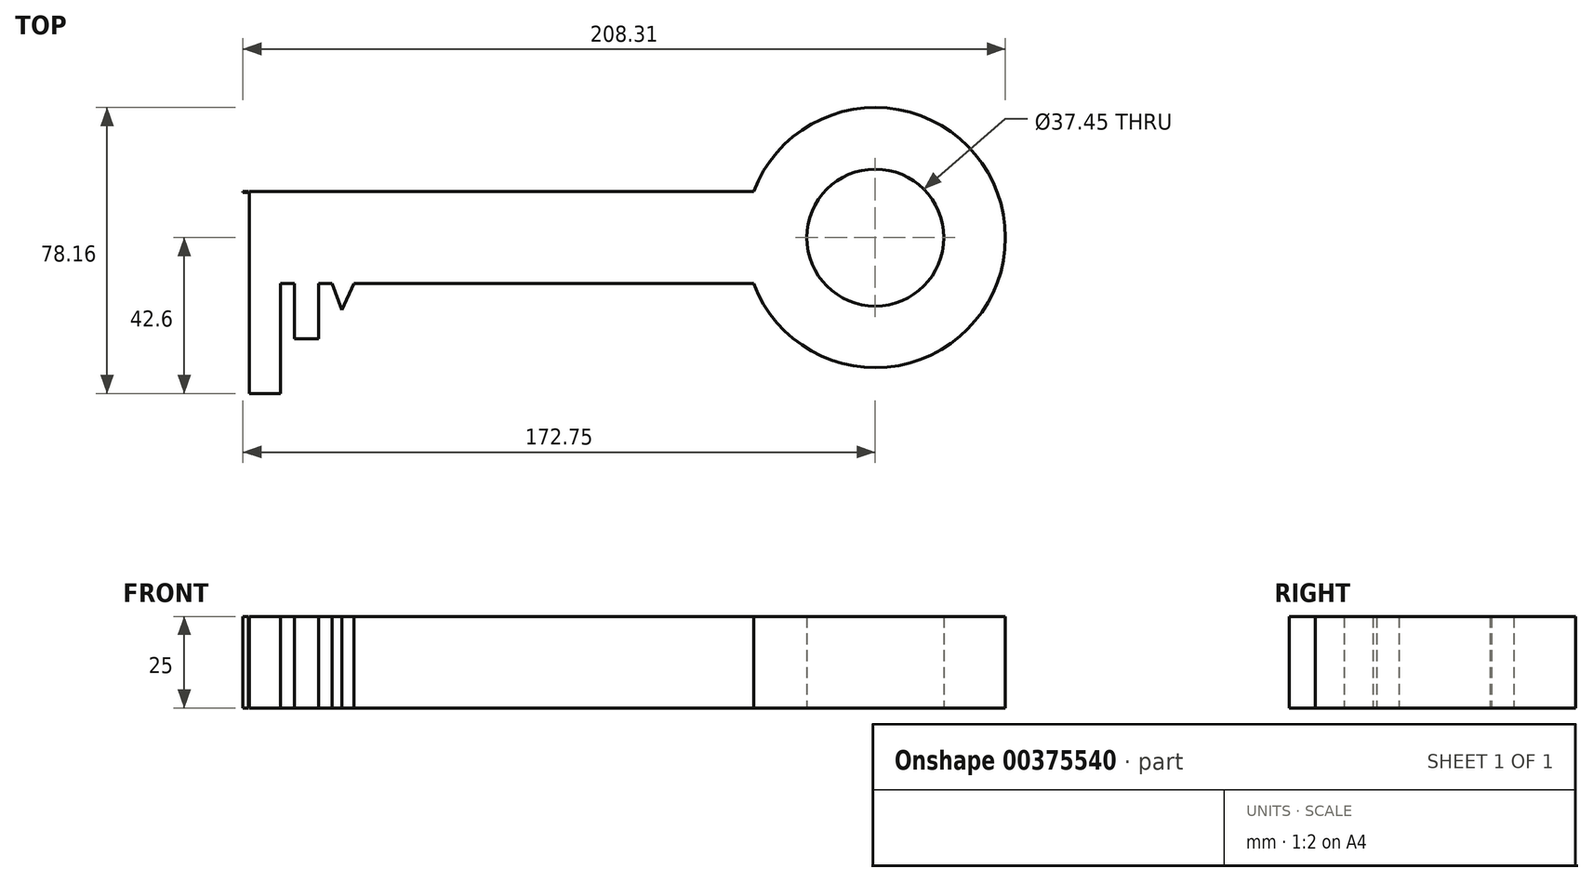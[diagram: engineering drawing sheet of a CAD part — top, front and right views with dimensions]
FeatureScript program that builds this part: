
annotation { "Feature Type Name" : "Feature", "Feature Type Description" : "" }
export const myFeature = defineFeature(function(context is Context, id is Id, definition is map)
    precondition{}
    {
        {
            var Q0;
            Q0=qCreatedBy(makeId("Top.planeOp"),FACE);
            var sketch = newSketch(context, id + "F0", { "sketchPlane" : qUnion([Q0])});
            skLineSegment(sketch, "E0.bottom", {"start": v(-68.4, 49.35) * mm, "end": v(-66.9, 49.35) * mm});
            skLineSegment(sketch, "E0.top", {"start": v(-68.4, 49.65) * mm, "end": v(-66.9, 49.65) * mm});
            skLineSegment(sketch, "E0.left", {"start": v(-68.4, 49.35) * mm, "end": v(-68.4, 49.65) * mm});
            skLineSegment(sketch, "E0.right", {"start": v(-66.9, 49.35) * mm, "end": v(-66.9, 49.65) * mm});
            skLineSegment(sketch, "E1.bottom", {"start": v(-66.6, 49.65) * mm, "end": v(71.1, 49.65) * mm});
            skLineSegment(sketch, "E1.top", {"start": v(-66.6, 24.45) * mm, "end": v(71.1, 24.45) * mm});
            skLineSegment(sketch, "E1.left", {"start": v(-66.6, 49.65) * mm, "end": v(-66.6, 24.45) * mm});
            skArc(sketch, "E2", {"start": v(71.1, 24.45) * mm, "mid": v(139.9, 37.05) * mm, "end": v(71.1, 49.65) * mm});
            skCircle(sketch, "E3", {"center": v(104.35, 37.05) * mm, "radius": 18.72 * mm});
            skLineSegment(sketch, "E4.bottom", {"start": v(-66.6, 24.45) * mm, "end": v(-58.2, 24.45) * mm});
            skLineSegment(sketch, "E4.top", {"start": v(-66.6, -5.55) * mm, "end": v(-58.2, -5.55) * mm});
            skLineSegment(sketch, "E4.left", {"start": v(-66.6, 24.45) * mm, "end": v(-66.6, -5.55) * mm});
            skLineSegment(sketch, "E4.right", {"start": v(-58.2, 24.45) * mm, "end": v(-58.2, -5.55) * mm});
            skLineSegment(sketch, "E5.bottom", {"start": v(-54.3, 24.45) * mm, "end": v(-47.7, 24.45) * mm});
            skLineSegment(sketch, "E5.top", {"start": v(-54.3, 9.45) * mm, "end": v(-47.7, 9.45) * mm});
            skLineSegment(sketch, "E5.left", {"start": v(-54.3, 24.45) * mm, "end": v(-54.3, 9.45) * mm});
            skLineSegment(sketch, "E5.right", {"start": v(-47.7, 24.45) * mm, "end": v(-47.7, 9.45) * mm});
            skLineSegment(sketch, "E6", {"start": v(-44.1, 24.45) * mm, "end": v(-41.4, 17.25) * mm});
            skLineSegment(sketch, "E7", {"start": v(-41.4, 17.25) * mm, "end": v(-38.1, 24.45) * mm});
            skSolve(sketch);
        }
        {
            var Q0;
            Q0 = qSketchRegion(id + "F0", true);
            extrude(context, id + "F1", {"entities" : qUnion([Q0]), "depth" : 25 * mm});
        }
    });
